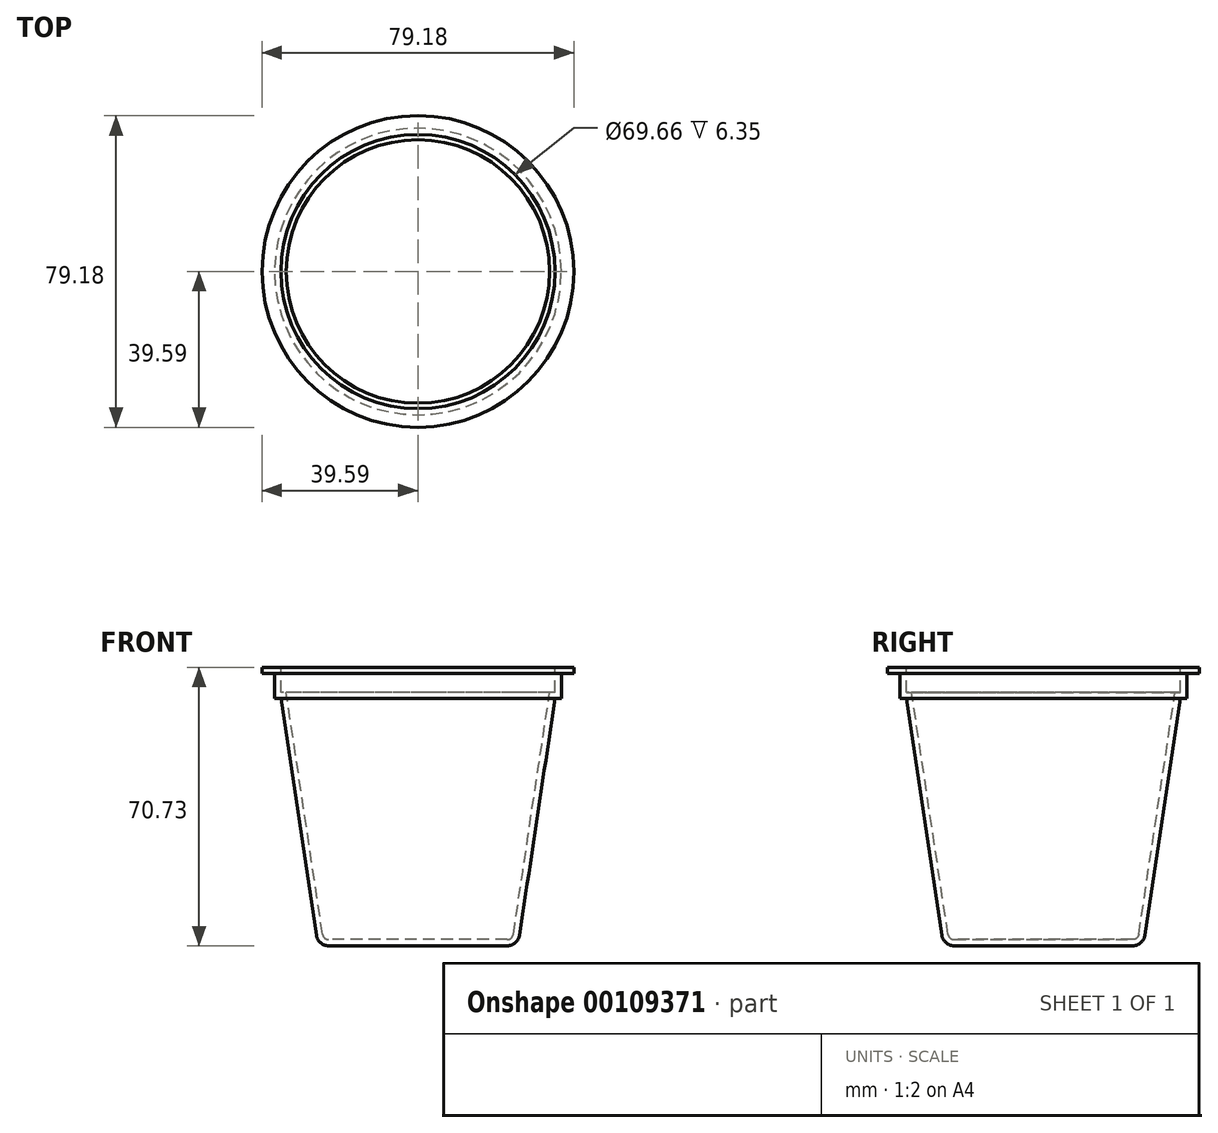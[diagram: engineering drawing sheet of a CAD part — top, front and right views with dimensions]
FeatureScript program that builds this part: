
annotation { "Feature Type Name" : "Feature", "Feature Type Description" : "" }
export const myFeature = defineFeature(function(context is Context, id is Id, definition is map)
    precondition{}
    {
        {
            var Q0;
            Q0=qCreatedBy(makeId("Front.planeOp"),FACE);
            var sketch = newSketch(context, id + "F0", { "sketchPlane" : qUnion([Q0])});
            skLineSegment(sketch, "E0", {"start": v(0, 0) * mm, "end": v(22.67, 0) * mm});
            skLineSegment(sketch, "E1", {"start": v(25.8, 2.7) * mm, "end": v(34.83, 62.8) * mm});
            skLineSegment(sketch, "E2", {"start": v(34.83, 62.8) * mm, "end": v(36.42, 62.8) * mm});
            skLineSegment(sketch, "E3", {"start": v(36.42, 62.8) * mm, "end": v(36.42, 69.15) * mm});
            skLineSegment(sketch, "E4", {"start": v(36.42, 69.15) * mm, "end": v(39.6, 69.15) * mm});
            skLineSegment(sketch, "E5", {"start": v(39.6, 69.15) * mm, "end": v(39.6, 70.73) * mm});
            skLineSegment(sketch, "E6", {"start": v(39.6, 70.73) * mm, "end": v(0, 70.73) * mm});
            skLineSegment(sketch, "E7", {"start": v(0, 70.73) * mm, "end": v(0, 0) * mm});
            skPoint(sketch, "E8.visualSharp", {"position": v(25.4, 0) * mm});
            skArc(sketch, "E8.filletArc", {"start": v(22.67, 0) * mm, "mid": v(24.74, 0.77) * mm, "end": v(25.8, 2.7) * mm});
            skSolve(sketch);
        }
        {
            var Q0;
            Q0 = qSketchRegion(id + "F0", true);
            var Q1;
            Q1=sQuery(id+"F0.wireOp",EDGE,"E7");
            revolve(context, id + "F1", {"entities" : qUnion([Q0]), "axis" : qUnion([Q1]), "revolveType" : RevolveType.FULL});
        }
        {
            var Q0;
            Q0=makeQuery(id+"F1.opRevolve","SWEPT_FACE",FACE,{"disambiguationData":[OSD([sQuery(id+"F0.wireOp",EDGE,"E6")])]});
            shell(context, id + "F2", {"entities" : qUnion([Q0]), "thickness" : 1.59 * mm});
        }
    });
